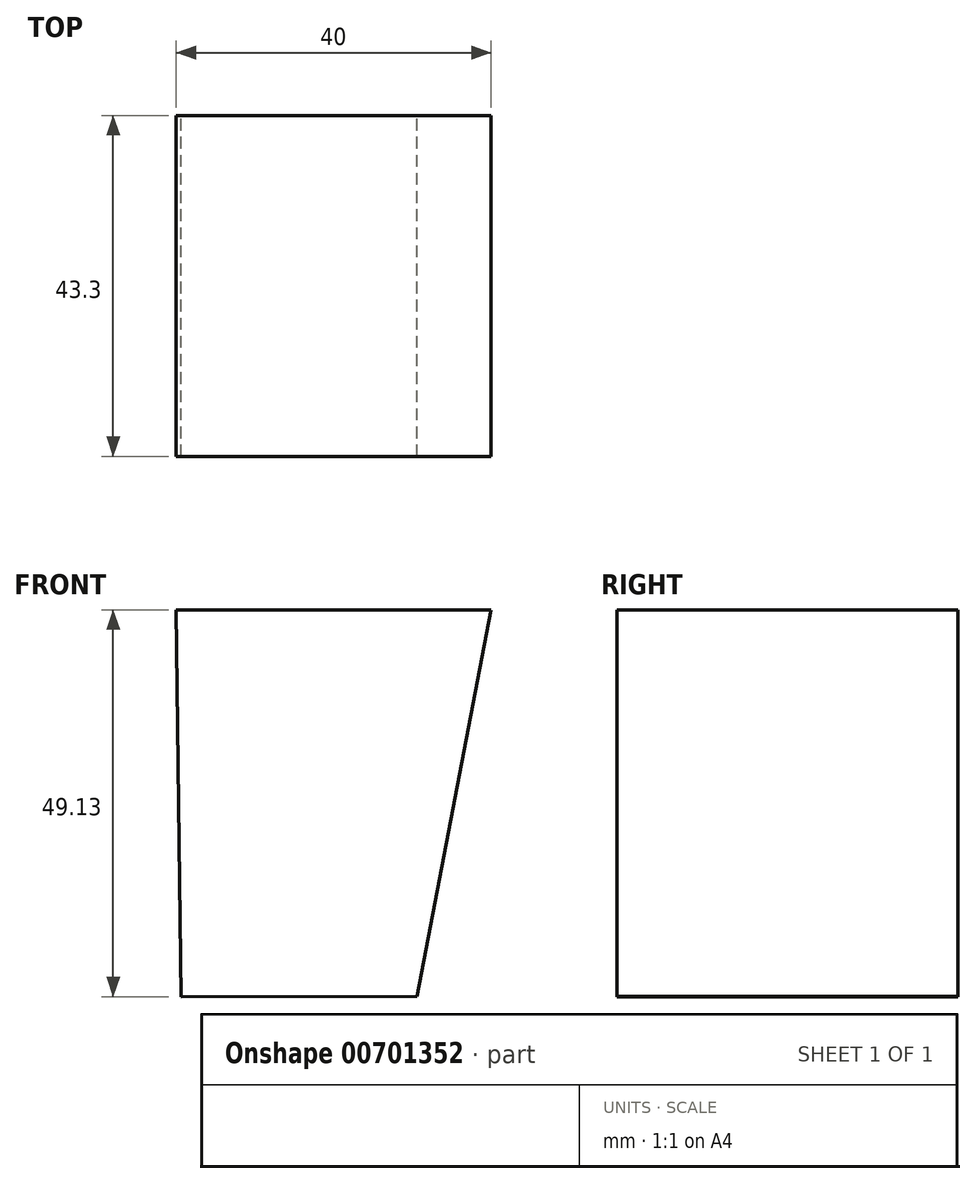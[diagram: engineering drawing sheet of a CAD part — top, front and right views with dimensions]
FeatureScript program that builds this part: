
annotation { "Feature Type Name" : "Feature", "Feature Type Description" : "" }
export const myFeature = defineFeature(function(context is Context, id is Id, definition is map)
    precondition{}
    {
        {
            var Q0;
            Q0=qCreatedBy(makeId("Front.planeOp"),FACE);
            var sketch = newSketch(context, id + "F0", { "sketchPlane" : qUnion([Q0])});
            skLineSegment(sketch, "E0.bottom", {"start": v(-24.82, 33.32) * mm, "end": v(15.18, 33.32) * mm});
            skLineSegment(sketch, "E0.top", {"start": v(-24.22, -15.81) * mm, "end": v(5.78, -15.79) * mm});
            skLineSegment(sketch, "E0.left", {"start": v(-24.82, 33.32) * mm, "end": v(-24.22, -15.81) * mm});
            skLineSegment(sketch, "E0.right", {"start": v(15.18, 33.32) * mm, "end": v(5.78, -15.79) * mm});
            skPoint(sketch, "E0.middle", {"position": v(-0.52, -2.63) * mm});
            skSolve(sketch);
        }
        {
            var Q0;
            Q0=makeQuery(id+"F0.imprint","IMPRINT",FACE,{"disambiguationData":[TD([[makeQuery(id+"F0.imprint","IMPRINT",EDGE,{"derivedFrom":sQuery(id+"F0.wireOp",EDGE,"E0.bottom")}),-1.0]])]});
            extrude(context, id + "F1", {"entities" : qUnion([Q0]), "depth" : 43.3 * mm, "offsetDistance" : 25 * mm});
        }
    });
